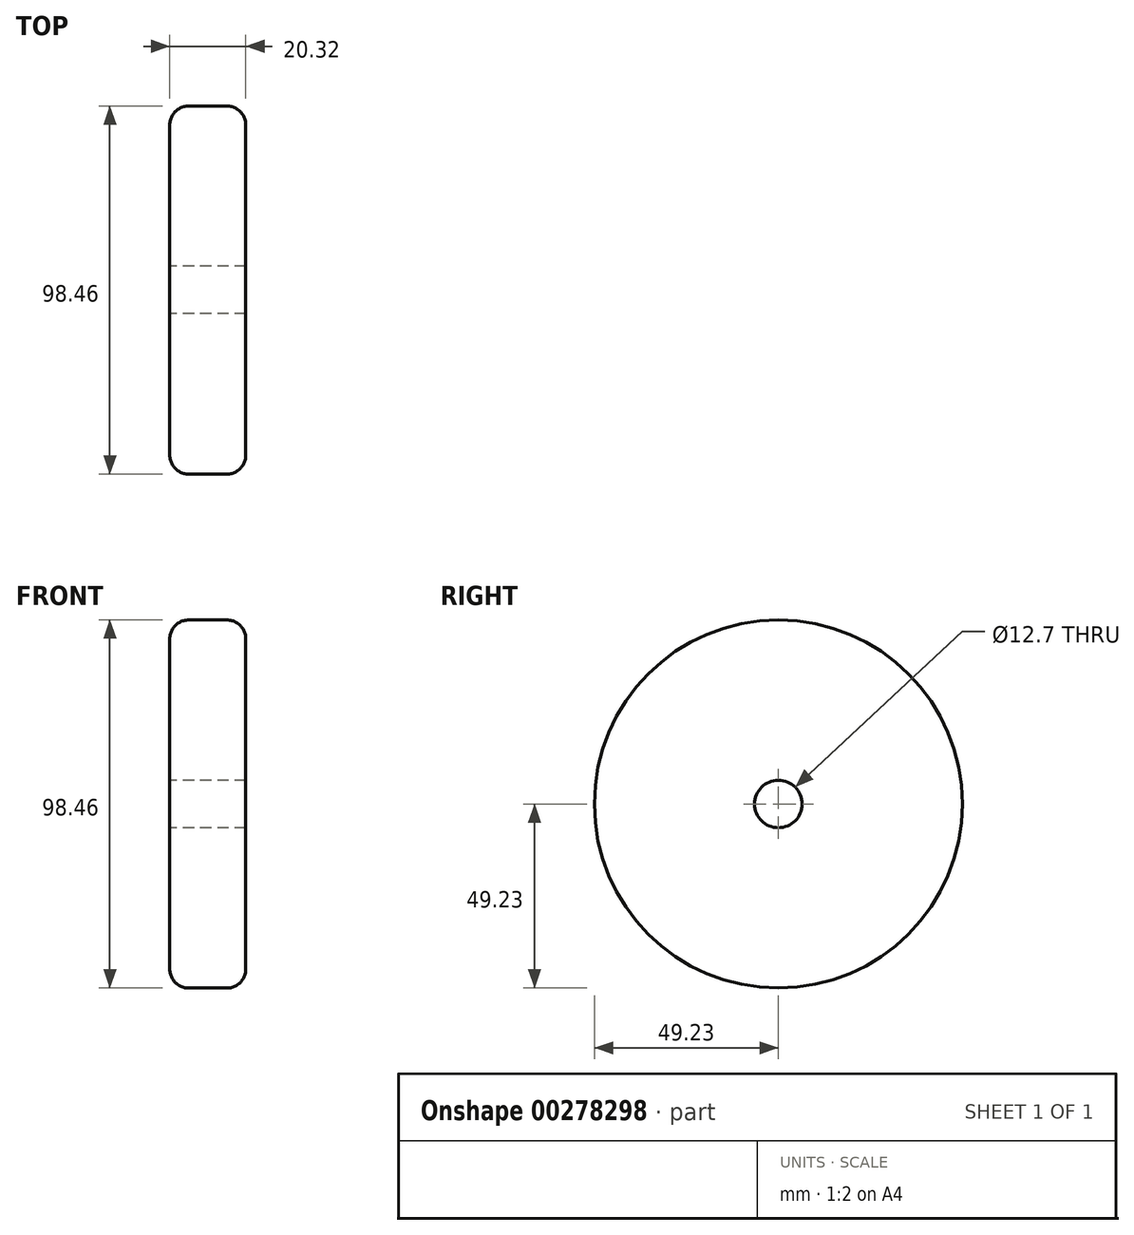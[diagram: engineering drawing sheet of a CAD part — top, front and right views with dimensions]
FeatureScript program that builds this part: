
annotation { "Feature Type Name" : "Feature", "Feature Type Description" : "" }
export const myFeature = defineFeature(function(context is Context, id is Id, definition is map)
    precondition{}
    {
        {
            var Q0;
            Q0=qCreatedBy(makeId("Right.planeOp"),FACE);
            var sketch = newSketch(context, id + "F0", { "sketchPlane" : qUnion([Q0])});
            skCircle(sketch, "E0", {"center": v(0, 0) * mm, "radius": 49.23 * mm});
            skCircle(sketch, "E1", {"center": v(0, 0) * mm, "radius": 6.35 * mm});
            skSolve(sketch);
        }
        {
            var Q0;
            Q0 = qSketchRegion(id + "F0", true);
            extrude(context, id + "F1", {"entities" : qUnion([Q0]), "depth" : 20.32 * mm});
        }
        {
            var Q0;
            Q0=makeQuery(id+"F1.opExtrude","CAP_EDGE",EDGE,{"disambiguationData":[OSD([sQuery(id+"F0.wireOp",EDGE,"E0")])],"isStart":true});
            var Q1;
            Q1=makeQuery(id+"F1.opExtrude","CAP_EDGE",EDGE,{"disambiguationData":[OSD([sQuery(id+"F0.wireOp",EDGE,"E0")])],"isStart":false});
            fillet(context, id + "F2", {"entities" : qUnion([Q0, Q1]), "radius" : 5.08 * mm, "tangentPropagation" : true, "allowEdgeOverflow" : false});
        }
    });
